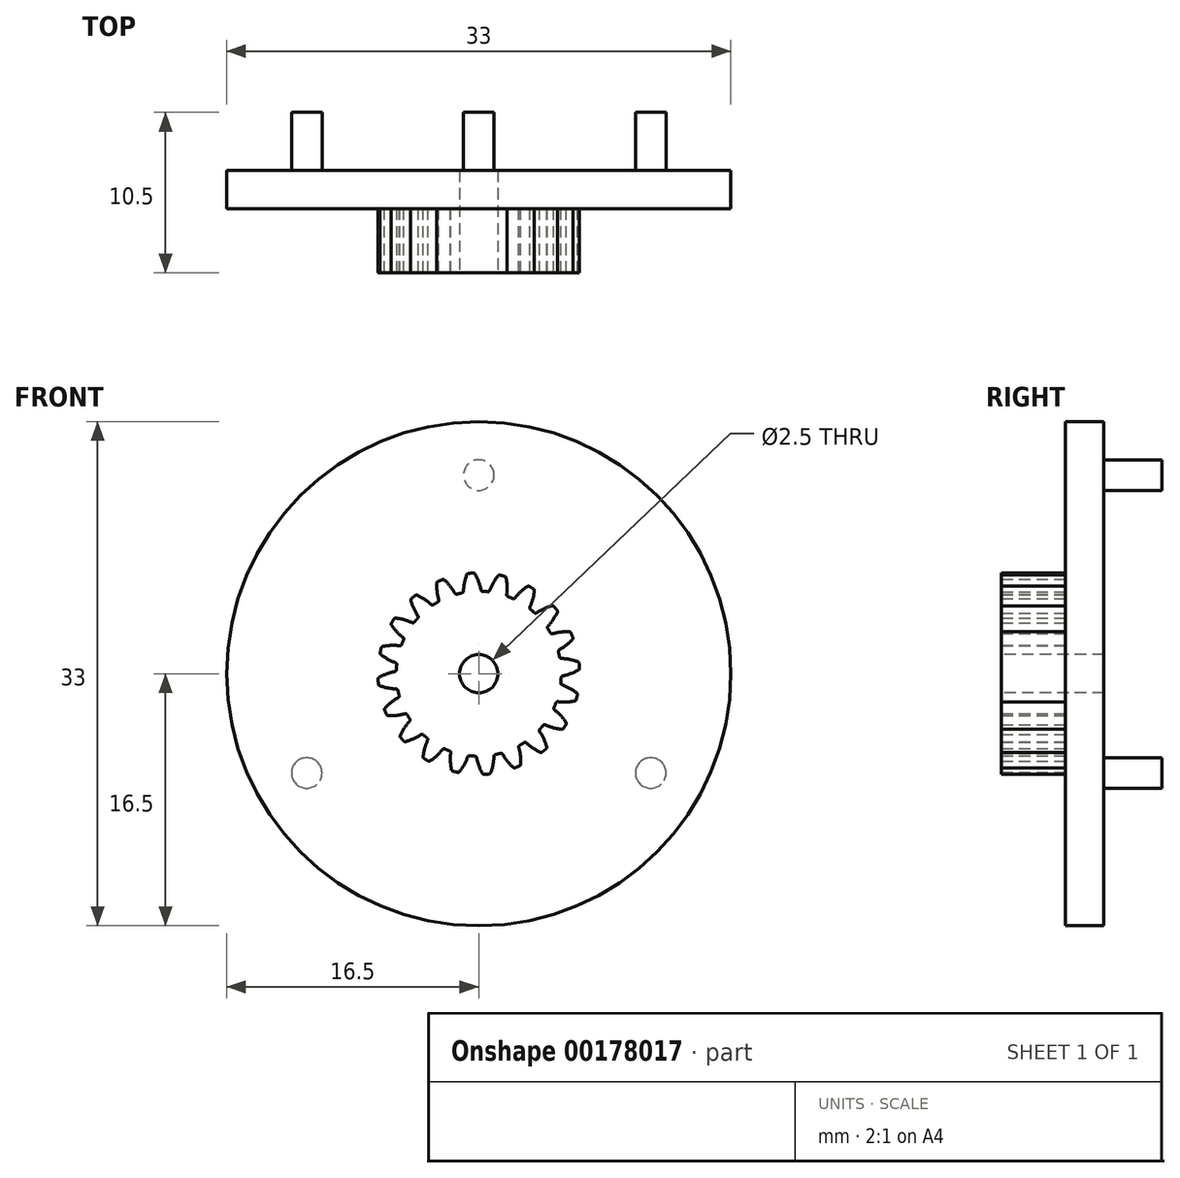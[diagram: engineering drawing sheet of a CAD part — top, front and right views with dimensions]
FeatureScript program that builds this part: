
annotation { "Feature Type Name" : "Feature", "Feature Type Description" : "" }
export const myFeature = defineFeature(function(context is Context, id is Id, definition is map)
    precondition{}
    {
        {
            var Q0;
            Q0=qCreatedBy(makeId("Front.planeOp"),FACE);
            var sketch = newSketch(context, id + "F0", { "sketchPlane" : qUnion([Q0])});
            skCircle(sketch, "E0", {"center": v(0, 0) * mm, "radius": 6 * mm, "construction": true});
            skCircle(sketch, "E1", {"center": v(0, 0) * mm, "radius": 5.4 * mm, "construction": true});
            skCircle(sketch, "E2", {"center": v(0, 0) * mm, "radius": 6.6 * mm, "construction": true});
            skLineSegment(sketch, "E3", {"start": v(0, 0) * mm, "end": v(0, 7.77) * mm, "construction": true});
            skPoint(sketch, "E4", {"position": v(0, 6) * mm});
            skLineSegment(sketch, "E5", {"start": v(0, 6) * mm, "end": v(-7.8, 6) * mm, "construction": true});
            skCircle(sketch, "E6.cCircle", {"center": v(0, 0) * mm, "radius": 7.77 * mm, "construction": true});
            skLineSegment(sketch, "E6.0", {"start": v(-0.61, 7.77) * mm, "end": v(0.61, 7.77) * mm, "construction": true});
            skLineSegment(sketch, "E6.1", {"start": v(0.61, 7.77) * mm, "end": v(1.82, 7.58) * mm, "construction": true});
            skLineSegment(sketch, "E6.2", {"start": v(1.82, 7.58) * mm, "end": v(2.98, 7.2) * mm, "construction": true});
            skLineSegment(sketch, "E6.3", {"start": v(2.98, 7.2) * mm, "end": v(4.07, 6.65) * mm, "construction": true});
            skLineSegment(sketch, "E6.4", {"start": v(4.07, 6.65) * mm, "end": v(5.06, 5.93) * mm, "construction": true});
            skLineSegment(sketch, "E6.5", {"start": v(5.06, 5.93) * mm, "end": v(5.93, 5.06) * mm, "construction": true});
            skLineSegment(sketch, "E6.6", {"start": v(5.93, 5.06) * mm, "end": v(6.65, 4.07) * mm, "construction": true});
            skLineSegment(sketch, "E6.7", {"start": v(6.65, 4.07) * mm, "end": v(7.2, 2.98) * mm, "construction": true});
            skLineSegment(sketch, "E6.8", {"start": v(7.2, 2.98) * mm, "end": v(7.58, 1.82) * mm, "construction": true});
            skLineSegment(sketch, "E6.9", {"start": v(7.58, 1.82) * mm, "end": v(7.77, 0.61) * mm, "construction": true});
            skLineSegment(sketch, "E6.10", {"start": v(7.77, 0.61) * mm, "end": v(7.77, -0.61) * mm, "construction": true});
            skLineSegment(sketch, "E6.11", {"start": v(7.77, -0.61) * mm, "end": v(7.58, -1.82) * mm, "construction": true});
            skLineSegment(sketch, "E6.12", {"start": v(7.58, -1.82) * mm, "end": v(7.2, -2.98) * mm, "construction": true});
            skLineSegment(sketch, "E6.13", {"start": v(7.2, -2.98) * mm, "end": v(6.65, -4.07) * mm, "construction": true});
            skLineSegment(sketch, "E6.14", {"start": v(6.65, -4.07) * mm, "end": v(5.93, -5.06) * mm, "construction": true});
            skLineSegment(sketch, "E6.15", {"start": v(5.93, -5.06) * mm, "end": v(5.06, -5.93) * mm, "construction": true});
            skLineSegment(sketch, "E6.16", {"start": v(5.06, -5.93) * mm, "end": v(4.07, -6.65) * mm, "construction": true});
            skLineSegment(sketch, "E6.17", {"start": v(4.07, -6.65) * mm, "end": v(2.98, -7.2) * mm, "construction": true});
            skLineSegment(sketch, "E6.18", {"start": v(2.98, -7.2) * mm, "end": v(1.82, -7.58) * mm, "construction": true});
            skLineSegment(sketch, "E6.19", {"start": v(1.82, -7.58) * mm, "end": v(0.61, -7.77) * mm, "construction": true});
            skLineSegment(sketch, "E6.20", {"start": v(0.61, -7.77) * mm, "end": v(-0.61, -7.77) * mm, "construction": true});
            skLineSegment(sketch, "E6.21", {"start": v(-0.61, -7.77) * mm, "end": v(-1.82, -7.58) * mm, "construction": true});
            skLineSegment(sketch, "E6.22", {"start": v(-1.82, -7.58) * mm, "end": v(-2.98, -7.2) * mm, "construction": true});
            skLineSegment(sketch, "E6.23", {"start": v(-2.98, -7.2) * mm, "end": v(-4.07, -6.65) * mm, "construction": true});
            skLineSegment(sketch, "E6.24", {"start": v(-4.07, -6.65) * mm, "end": v(-5.06, -5.93) * mm, "construction": true});
            skLineSegment(sketch, "E6.25", {"start": v(-5.06, -5.93) * mm, "end": v(-5.93, -5.06) * mm, "construction": true});
            skLineSegment(sketch, "E6.26", {"start": v(-5.93, -5.06) * mm, "end": v(-6.65, -4.07) * mm, "construction": true});
            skLineSegment(sketch, "E6.27", {"start": v(-6.65, -4.07) * mm, "end": v(-7.2, -2.98) * mm, "construction": true});
            skLineSegment(sketch, "E6.28", {"start": v(-7.2, -2.98) * mm, "end": v(-7.58, -1.82) * mm, "construction": true});
            skLineSegment(sketch, "E6.29", {"start": v(-7.58, -1.82) * mm, "end": v(-7.77, -0.61) * mm, "construction": true});
            skLineSegment(sketch, "E6.30", {"start": v(-7.77, -0.61) * mm, "end": v(-7.77, 0.61) * mm, "construction": true});
            skLineSegment(sketch, "E6.31", {"start": v(-7.77, 0.61) * mm, "end": v(-7.58, 1.82) * mm, "construction": true});
            skLineSegment(sketch, "E6.32", {"start": v(-7.58, 1.82) * mm, "end": v(-7.2, 2.98) * mm, "construction": true});
            skLineSegment(sketch, "E6.33", {"start": v(-7.2, 2.98) * mm, "end": v(-6.65, 4.07) * mm, "construction": true});
            skLineSegment(sketch, "E6.34", {"start": v(-6.65, 4.07) * mm, "end": v(-5.93, 5.06) * mm, "construction": true});
            skLineSegment(sketch, "E6.35", {"start": v(-5.93, 5.06) * mm, "end": v(-5.06, 5.93) * mm, "construction": true});
            skLineSegment(sketch, "E6.36", {"start": v(-5.06, 5.93) * mm, "end": v(-4.07, 6.65) * mm, "construction": true});
            skLineSegment(sketch, "E6.37", {"start": v(-4.07, 6.65) * mm, "end": v(-2.98, 7.2) * mm, "construction": true});
            skLineSegment(sketch, "E6.38", {"start": v(-2.98, 7.2) * mm, "end": v(-1.82, 7.58) * mm, "construction": true});
            skLineSegment(sketch, "E6.39", {"start": v(-1.82, 7.58) * mm, "end": v(-0.61, 7.77) * mm, "construction": true});
            skPoint(sketch, "E6.0.midPoint", {"position": v(0, 7.77) * mm});
            skLineSegment(sketch, "E7.0", {"start": v(0, 7.77) * mm, "end": v(1.22, 7.68) * mm, "construction": true});
            skLineSegment(sketch, "E7.1", {"start": v(1.22, 7.68) * mm, "end": v(2.4, 7.4) * mm, "construction": true});
            skLineSegment(sketch, "E7.2", {"start": v(2.4, 7.4) * mm, "end": v(3.53, 6.93) * mm, "construction": true});
            skLineSegment(sketch, "E7.3", {"start": v(3.53, 6.93) * mm, "end": v(4.57, 6.29) * mm, "construction": true});
            skLineSegment(sketch, "E7.4", {"start": v(4.57, 6.29) * mm, "end": v(5.5, 5.5) * mm, "construction": true});
            skLineSegment(sketch, "E7.5", {"start": v(5.5, 5.5) * mm, "end": v(6.29, 4.57) * mm, "construction": true});
            skLineSegment(sketch, "E7.6", {"start": v(6.29, 4.57) * mm, "end": v(6.93, 3.53) * mm, "construction": true});
            skLineSegment(sketch, "E7.7", {"start": v(6.93, 3.53) * mm, "end": v(7.4, 2.4) * mm, "construction": true});
            skLineSegment(sketch, "E7.8", {"start": v(7.4, 2.4) * mm, "end": v(7.68, 1.22) * mm, "construction": true});
            skLineSegment(sketch, "E7.9", {"start": v(7.68, 1.22) * mm, "end": v(7.77, 0) * mm, "construction": true});
            skLineSegment(sketch, "E7.10", {"start": v(7.77, 0) * mm, "end": v(7.68, -1.22) * mm, "construction": true});
            skLineSegment(sketch, "E7.11", {"start": v(7.68, -1.22) * mm, "end": v(7.4, -2.4) * mm, "construction": true});
            skLineSegment(sketch, "E7.12", {"start": v(7.4, -2.4) * mm, "end": v(6.93, -3.53) * mm, "construction": true});
            skLineSegment(sketch, "E7.13", {"start": v(6.93, -3.53) * mm, "end": v(6.29, -4.57) * mm, "construction": true});
            skLineSegment(sketch, "E7.14", {"start": v(6.29, -4.57) * mm, "end": v(5.5, -5.5) * mm, "construction": true});
            skLineSegment(sketch, "E7.15", {"start": v(5.5, -5.5) * mm, "end": v(4.57, -6.29) * mm, "construction": true});
            skLineSegment(sketch, "E7.16", {"start": v(4.57, -6.29) * mm, "end": v(3.53, -6.93) * mm, "construction": true});
            skLineSegment(sketch, "E7.17", {"start": v(3.53, -6.93) * mm, "end": v(2.4, -7.4) * mm, "construction": true});
            skLineSegment(sketch, "E7.18", {"start": v(2.4, -7.4) * mm, "end": v(1.22, -7.68) * mm, "construction": true});
            skLineSegment(sketch, "E7.19", {"start": v(1.22, -7.68) * mm, "end": v(0, -7.77) * mm, "construction": true});
            skLineSegment(sketch, "E7.20", {"start": v(0, -7.77) * mm, "end": v(-1.22, -7.68) * mm, "construction": true});
            skLineSegment(sketch, "E7.21", {"start": v(-1.22, -7.68) * mm, "end": v(-2.4, -7.4) * mm, "construction": true});
            skLineSegment(sketch, "E7.22", {"start": v(-2.4, -7.4) * mm, "end": v(-3.53, -6.93) * mm, "construction": true});
            skLineSegment(sketch, "E7.23", {"start": v(-3.53, -6.93) * mm, "end": v(-4.57, -6.29) * mm, "construction": true});
            skLineSegment(sketch, "E7.24", {"start": v(-4.57, -6.29) * mm, "end": v(-5.5, -5.5) * mm, "construction": true});
            skLineSegment(sketch, "E7.25", {"start": v(-5.5, -5.5) * mm, "end": v(-6.29, -4.57) * mm, "construction": true});
            skLineSegment(sketch, "E7.26", {"start": v(-6.29, -4.57) * mm, "end": v(-6.93, -3.53) * mm, "construction": true});
            skLineSegment(sketch, "E7.27", {"start": v(-6.93, -3.53) * mm, "end": v(-7.4, -2.4) * mm, "construction": true});
            skLineSegment(sketch, "E7.28", {"start": v(-7.4, -2.4) * mm, "end": v(-7.68, -1.22) * mm, "construction": true});
            skLineSegment(sketch, "E7.29", {"start": v(-7.68, -1.22) * mm, "end": v(-7.77, 0) * mm, "construction": true});
            skLineSegment(sketch, "E7.30", {"start": v(-7.77, 0) * mm, "end": v(-7.68, 1.22) * mm, "construction": true});
            skLineSegment(sketch, "E7.31", {"start": v(-7.68, 1.22) * mm, "end": v(-7.4, 2.4) * mm, "construction": true});
            skLineSegment(sketch, "E7.32", {"start": v(-7.4, 2.4) * mm, "end": v(-6.93, 3.53) * mm, "construction": true});
            skLineSegment(sketch, "E7.33", {"start": v(-6.93, 3.53) * mm, "end": v(-6.29, 4.57) * mm, "construction": true});
            skLineSegment(sketch, "E7.34", {"start": v(-6.29, 4.57) * mm, "end": v(-5.5, 5.5) * mm, "construction": true});
            skLineSegment(sketch, "E7.35", {"start": v(-5.5, 5.5) * mm, "end": v(-4.57, 6.29) * mm, "construction": true});
            skLineSegment(sketch, "E7.36", {"start": v(-4.57, 6.29) * mm, "end": v(-3.53, 6.93) * mm, "construction": true});
            skLineSegment(sketch, "E7.37", {"start": v(-3.53, 6.93) * mm, "end": v(-2.4, 7.4) * mm, "construction": true});
            skLineSegment(sketch, "E7.38", {"start": v(-2.4, 7.4) * mm, "end": v(-1.22, 7.68) * mm, "construction": true});
            skLineSegment(sketch, "E7.39", {"start": v(-1.22, 7.68) * mm, "end": v(0, 7.77) * mm, "construction": true});
            skLineSegment(sketch, "E8", {"start": v(0, 0) * mm, "end": v(-0.61, 7.77) * mm, "construction": true});
            skLineSegment(sketch, "E9", {"start": v(0, 6) * mm, "end": v(-7.35, 3.32) * mm, "construction": true});
            skCircle(sketch, "E10", {"center": v(0, 6) * mm, "radius": 3.6 * mm, "construction": true});
            skPoint(sketch, "E11", {"position": v(-3.38, 4.77) * mm});
            skCircle(sketch, "E12", {"center": v(-3.38, 4.77) * mm, "radius": 3.6 * mm, "construction": true});
            skArc(sketch, "E13", {"start": v(-0.24, 6.53) * mm, "mid": v(0, 6.02) * mm, "end": v(0.14, 5.49) * mm});
            skArc(sketch, "E14.MirrorCS", {"start": v(-0.78, 6.49) * mm, "mid": v(-0.93, 5.95) * mm, "end": v(-1, 5.4) * mm});
            skArc(sketch, "E15", {"start": v(-0.68, 6.56) * mm, "mid": v(-0.52, 6.58) * mm, "end": v(-0.35, 6.6) * mm});
            skArc(sketch, "E16", {"start": v(-1.1, 5.29) * mm, "mid": v(0.42, -5.38) * mm, "end": v(0.26, 5.4) * mm});
            skPoint(sketch, "E17.visualSharp", {"position": v(-1, 5.3) * mm});
            skArc(sketch, "E17.filletArc", {"start": v(-1.1, 5.29) * mm, "mid": v(-1.03, 5.33) * mm, "end": v(-1, 5.4) * mm});
            skPoint(sketch, "E18.visualSharp", {"position": v(0.16, 5.4) * mm});
            skArc(sketch, "E18.filletArc", {"start": v(0.14, 5.49) * mm, "mid": v(0.18, 5.42) * mm, "end": v(0.26, 5.4) * mm});
            skPoint(sketch, "E19.visualSharp", {"position": v(-0.76, 6.56) * mm});
            skArc(sketch, "E19.filletArc", {"start": v(-0.68, 6.56) * mm, "mid": v(-0.74, 6.54) * mm, "end": v(-0.78, 6.49) * mm});
            skPoint(sketch, "E20.visualSharp", {"position": v(-0.28, 6.6) * mm});
            skArc(sketch, "E20.filletArc", {"start": v(-0.24, 6.53) * mm, "mid": v(-0.29, 6.58) * mm, "end": v(-0.35, 6.6) * mm});
            skLineSegment(sketch, "E21", {"start": v(0, 0) * mm, "end": v(-1.44, 6.92) * mm, "construction": true});
            skPoint(sketch, "E22.1.0", {"position": v(-1.51, 5.18) * mm});
            skPoint(sketch, "E22.1.1", {"position": v(-1.85, 5.7) * mm});
            skArc(sketch, "E22.1.2", {"start": v(-2.25, 6.13) * mm, "mid": v(-1.87, 5.73) * mm, "end": v(-1.56, 5.27) * mm});
            skArc(sketch, "E22.1.3", {"start": v(-2.68, 6.03) * mm, "mid": v(-2.53, 6.1) * mm, "end": v(-2.37, 6.16) * mm});
            skPoint(sketch, "E22.1.4", {"position": v(-2.3, 6.18) * mm});
            skPoint(sketch, "E22.1.5", {"position": v(-2.6, 4.74) * mm});
            skArc(sketch, "E22.1.6", {"start": v(-2.75, 5.93) * mm, "mid": v(-2.73, 5.37) * mm, "end": v(-2.62, 4.83) * mm});
            skPoint(sketch, "E22.1.7", {"position": v(-2.74, 6) * mm});
            skArc(sketch, "E22.1.8", {"start": v(-1.56, 5.27) * mm, "mid": v(-1.5, 5.21) * mm, "end": v(-1.42, 5.2) * mm});
            skArc(sketch, "E22.1.9", {"start": v(-2.68, 6.03) * mm, "mid": v(-2.73, 6) * mm, "end": v(-2.75, 5.93) * mm});
            skArc(sketch, "E22.1.10", {"start": v(-2.68, 4.69) * mm, "mid": v(-2.63, 4.75) * mm, "end": v(-2.62, 4.83) * mm});
            skArc(sketch, "E22.1.11", {"start": v(-2.25, 6.13) * mm, "mid": v(-2.3, 6.16) * mm, "end": v(-2.37, 6.16) * mm});
            skPoint(sketch, "E22.2.0", {"position": v(-3.04, 4.46) * mm});
            skPoint(sketch, "E22.2.1", {"position": v(-3.53, 4.85) * mm});
            skArc(sketch, "E22.2.2", {"start": v(-4.03, 5.14) * mm, "mid": v(-3.55, 4.87) * mm, "end": v(-3.11, 4.53) * mm});
            skArc(sketch, "E22.2.3", {"start": v(-4.4, 4.91) * mm, "mid": v(-4.29, 5.02) * mm, "end": v(-4.16, 5.12) * mm});
            skPoint(sketch, "E22.2.4", {"position": v(-4.1, 5.17) * mm});
            skPoint(sketch, "E22.2.5", {"position": v(-3.93, 3.7) * mm});
            skArc(sketch, "E22.2.6", {"start": v(-4.45, 4.79) * mm, "mid": v(-4.25, 4.27) * mm, "end": v(-3.98, 3.78) * mm});
            skPoint(sketch, "E22.2.7", {"position": v(-4.46, 4.86) * mm});
            skArc(sketch, "E22.2.8", {"start": v(-3.11, 4.53) * mm, "mid": v(-3.04, 4.5) * mm, "end": v(-2.96, 4.51) * mm});
            skArc(sketch, "E22.2.9", {"start": v(-4.4, 4.91) * mm, "mid": v(-4.45, 4.85) * mm, "end": v(-4.45, 4.79) * mm});
            skArc(sketch, "E22.2.10", {"start": v(-4, 3.63) * mm, "mid": v(-3.96, 3.7) * mm, "end": v(-3.98, 3.78) * mm});
            skArc(sketch, "E22.2.11", {"start": v(-4.03, 5.14) * mm, "mid": v(-4.1, 5.15) * mm, "end": v(-4.16, 5.12) * mm});
            skPoint(sketch, "E22.3.0", {"position": v(-4.27, 3.3) * mm});
            skPoint(sketch, "E22.3.1", {"position": v(-4.85, 3.53) * mm});
            skArc(sketch, "E22.3.2", {"start": v(-5.43, 3.64) * mm, "mid": v(-4.88, 3.53) * mm, "end": v(-4.36, 3.34) * mm});
            skArc(sketch, "E22.3.3", {"start": v(-5.71, 3.3) * mm, "mid": v(-5.63, 3.45) * mm, "end": v(-5.54, 3.59) * mm});
            skPoint(sketch, "E22.3.4", {"position": v(-5.5, 3.65) * mm});
            skPoint(sketch, "E22.3.5", {"position": v(-4.88, 2.3) * mm});
            skArc(sketch, "E22.3.6", {"start": v(-5.7, 3.18) * mm, "mid": v(-5.36, 2.74) * mm, "end": v(-4.96, 2.36) * mm});
            skPoint(sketch, "E22.3.7", {"position": v(-5.75, 3.24) * mm});
            skArc(sketch, "E22.3.8", {"start": v(-4.36, 3.34) * mm, "mid": v(-4.28, 3.34) * mm, "end": v(-4.21, 3.38) * mm});
            skArc(sketch, "E22.3.9", {"start": v(-5.71, 3.3) * mm, "mid": v(-5.73, 3.24) * mm, "end": v(-5.7, 3.18) * mm});
            skArc(sketch, "E22.3.10", {"start": v(-4.92, 2.22) * mm, "mid": v(-4.92, 2.3) * mm, "end": v(-4.96, 2.36) * mm});
            skArc(sketch, "E22.3.11", {"start": v(-5.43, 3.64) * mm, "mid": v(-5.5, 3.63) * mm, "end": v(-5.54, 3.59) * mm});
            skPoint(sketch, "E22.4.0", {"position": v(-5.08, 1.82) * mm});
            skPoint(sketch, "E22.4.1", {"position": v(-5.7, 1.85) * mm});
            skArc(sketch, "E22.4.2", {"start": v(-6.28, 1.79) * mm, "mid": v(-5.73, 1.85) * mm, "end": v(-5.18, 1.83) * mm});
            skArc(sketch, "E22.4.3", {"start": v(-6.45, 1.38) * mm, "mid": v(-6.42, 1.54) * mm, "end": v(-6.38, 1.7) * mm});
            skPoint(sketch, "E22.4.4", {"position": v(-6.36, 1.77) * mm});
            skPoint(sketch, "E22.4.5", {"position": v(-5.36, 0.68) * mm});
            skArc(sketch, "E22.4.6", {"start": v(-6.41, 1.26) * mm, "mid": v(-5.95, 0.95) * mm, "end": v(-5.44, 0.72) * mm});
            skPoint(sketch, "E22.4.7", {"position": v(-6.47, 1.3) * mm});
            skArc(sketch, "E22.4.8", {"start": v(-5.18, 1.83) * mm, "mid": v(-5.1, 1.85) * mm, "end": v(-5.05, 1.91) * mm});
            skArc(sketch, "E22.4.9", {"start": v(-6.45, 1.38) * mm, "mid": v(-6.45, 1.31) * mm, "end": v(-6.41, 1.26) * mm});
            skArc(sketch, "E22.4.10", {"start": v(-5.37, 0.6) * mm, "mid": v(-5.38, 0.67) * mm, "end": v(-5.44, 0.72) * mm});
            skArc(sketch, "E22.4.11", {"start": v(-6.28, 1.79) * mm, "mid": v(-6.34, 1.76) * mm, "end": v(-6.38, 1.7) * mm});
            skPoint(sketch, "E22.5.0", {"position": v(-5.4, 0.16) * mm});
            skPoint(sketch, "E22.5.1", {"position": v(-6, 0) * mm});
            skArc(sketch, "E22.5.2", {"start": v(-6.53, -0.24) * mm, "mid": v(-6.02, 0) * mm, "end": v(-5.49, 0.14) * mm});
            skArc(sketch, "E22.5.3", {"start": v(-6.56, -0.68) * mm, "mid": v(-6.58, -0.52) * mm, "end": v(-6.6, -0.35) * mm});
            skPoint(sketch, "E22.5.4", {"position": v(-6.6, -0.28) * mm});
            skPoint(sketch, "E22.5.5", {"position": v(-5.3, -1) * mm});
            skArc(sketch, "E22.5.6", {"start": v(-6.49, -0.78) * mm, "mid": v(-5.95, -0.93) * mm, "end": v(-5.4, -1) * mm});
            skPoint(sketch, "E22.5.7", {"position": v(-6.56, -0.76) * mm});
            skArc(sketch, "E22.5.8", {"start": v(-5.49, 0.14) * mm, "mid": v(-5.42, 0.18) * mm, "end": v(-5.4, 0.26) * mm});
            skArc(sketch, "E22.5.9", {"start": v(-6.56, -0.68) * mm, "mid": v(-6.54, -0.74) * mm, "end": v(-6.49, -0.78) * mm});
            skArc(sketch, "E22.5.10", {"start": v(-5.29, -1.1) * mm, "mid": v(-5.33, -1.03) * mm, "end": v(-5.4, -1) * mm});
            skArc(sketch, "E22.5.11", {"start": v(-6.53, -0.24) * mm, "mid": v(-6.58, -0.29) * mm, "end": v(-6.6, -0.35) * mm});
            skPoint(sketch, "E22.6.0", {"position": v(-5.18, -1.51) * mm});
            skPoint(sketch, "E22.6.1", {"position": v(-5.7, -1.85) * mm});
            skArc(sketch, "E22.6.2", {"start": v(-6.13, -2.25) * mm, "mid": v(-5.73, -1.87) * mm, "end": v(-5.27, -1.56) * mm});
            skArc(sketch, "E22.6.3", {"start": v(-6.03, -2.68) * mm, "mid": v(-6.1, -2.53) * mm, "end": v(-6.16, -2.37) * mm});
            skPoint(sketch, "E22.6.4", {"position": v(-6.18, -2.3) * mm});
            skPoint(sketch, "E22.6.5", {"position": v(-4.74, -2.6) * mm});
            skArc(sketch, "E22.6.6", {"start": v(-5.93, -2.75) * mm, "mid": v(-5.37, -2.73) * mm, "end": v(-4.83, -2.62) * mm});
            skPoint(sketch, "E22.6.7", {"position": v(-6, -2.74) * mm});
            skArc(sketch, "E22.6.8", {"start": v(-5.27, -1.56) * mm, "mid": v(-5.21, -1.5) * mm, "end": v(-5.2, -1.42) * mm});
            skArc(sketch, "E22.6.9", {"start": v(-6.03, -2.68) * mm, "mid": v(-6, -2.73) * mm, "end": v(-5.93, -2.75) * mm});
            skArc(sketch, "E22.6.10", {"start": v(-4.69, -2.68) * mm, "mid": v(-4.75, -2.63) * mm, "end": v(-4.83, -2.62) * mm});
            skArc(sketch, "E22.6.11", {"start": v(-6.13, -2.25) * mm, "mid": v(-6.16, -2.3) * mm, "end": v(-6.16, -2.37) * mm});
            skPoint(sketch, "E22.7.0", {"position": v(-4.46, -3.04) * mm});
            skPoint(sketch, "E22.7.1", {"position": v(-4.85, -3.53) * mm});
            skArc(sketch, "E22.7.2", {"start": v(-5.14, -4.03) * mm, "mid": v(-4.87, -3.55) * mm, "end": v(-4.53, -3.11) * mm});
            skArc(sketch, "E22.7.3", {"start": v(-4.91, -4.4) * mm, "mid": v(-5.02, -4.29) * mm, "end": v(-5.12, -4.16) * mm});
            skPoint(sketch, "E22.7.4", {"position": v(-5.17, -4.1) * mm});
            skPoint(sketch, "E22.7.5", {"position": v(-3.7, -3.93) * mm});
            skArc(sketch, "E22.7.6", {"start": v(-4.79, -4.45) * mm, "mid": v(-4.27, -4.25) * mm, "end": v(-3.78, -3.98) * mm});
            skPoint(sketch, "E22.7.7", {"position": v(-4.86, -4.46) * mm});
            skArc(sketch, "E22.7.8", {"start": v(-4.53, -3.11) * mm, "mid": v(-4.5, -3.04) * mm, "end": v(-4.51, -2.96) * mm});
            skArc(sketch, "E22.7.9", {"start": v(-4.91, -4.4) * mm, "mid": v(-4.85, -4.45) * mm, "end": v(-4.79, -4.45) * mm});
            skArc(sketch, "E22.7.10", {"start": v(-3.63, -4) * mm, "mid": v(-3.7, -3.96) * mm, "end": v(-3.78, -3.98) * mm});
            skArc(sketch, "E22.7.11", {"start": v(-5.14, -4.03) * mm, "mid": v(-5.15, -4.1) * mm, "end": v(-5.12, -4.16) * mm});
            skPoint(sketch, "E22.8.0", {"position": v(-3.3, -4.27) * mm});
            skPoint(sketch, "E22.8.1", {"position": v(-3.53, -4.85) * mm});
            skArc(sketch, "E22.8.2", {"start": v(-3.64, -5.43) * mm, "mid": v(-3.53, -4.88) * mm, "end": v(-3.34, -4.36) * mm});
            skArc(sketch, "E22.8.3", {"start": v(-3.3, -5.71) * mm, "mid": v(-3.45, -5.63) * mm, "end": v(-3.59, -5.54) * mm});
            skPoint(sketch, "E22.8.4", {"position": v(-3.65, -5.5) * mm});
            skPoint(sketch, "E22.8.5", {"position": v(-2.3, -4.88) * mm});
            skArc(sketch, "E22.8.6", {"start": v(-3.18, -5.7) * mm, "mid": v(-2.74, -5.36) * mm, "end": v(-2.36, -4.96) * mm});
            skPoint(sketch, "E22.8.7", {"position": v(-3.24, -5.75) * mm});
            skArc(sketch, "E22.8.8", {"start": v(-3.34, -4.36) * mm, "mid": v(-3.34, -4.28) * mm, "end": v(-3.38, -4.21) * mm});
            skArc(sketch, "E22.8.9", {"start": v(-3.3, -5.71) * mm, "mid": v(-3.24, -5.73) * mm, "end": v(-3.18, -5.7) * mm});
            skArc(sketch, "E22.8.10", {"start": v(-2.22, -4.92) * mm, "mid": v(-2.3, -4.92) * mm, "end": v(-2.36, -4.96) * mm});
            skArc(sketch, "E22.8.11", {"start": v(-3.64, -5.43) * mm, "mid": v(-3.63, -5.5) * mm, "end": v(-3.59, -5.54) * mm});
            skPoint(sketch, "E22.9.0", {"position": v(-1.82, -5.08) * mm});
            skPoint(sketch, "E22.9.1", {"position": v(-1.85, -5.7) * mm});
            skArc(sketch, "E22.9.2", {"start": v(-1.79, -6.28) * mm, "mid": v(-1.85, -5.73) * mm, "end": v(-1.83, -5.18) * mm});
            skArc(sketch, "E22.9.3", {"start": v(-1.38, -6.45) * mm, "mid": v(-1.54, -6.42) * mm, "end": v(-1.7, -6.38) * mm});
            skPoint(sketch, "E22.9.4", {"position": v(-1.77, -6.36) * mm});
            skPoint(sketch, "E22.9.5", {"position": v(-0.68, -5.36) * mm});
            skArc(sketch, "E22.9.6", {"start": v(-1.26, -6.41) * mm, "mid": v(-0.95, -5.95) * mm, "end": v(-0.72, -5.44) * mm});
            skPoint(sketch, "E22.9.7", {"position": v(-1.3, -6.47) * mm});
            skArc(sketch, "E22.9.8", {"start": v(-1.83, -5.18) * mm, "mid": v(-1.85, -5.1) * mm, "end": v(-1.91, -5.05) * mm});
            skArc(sketch, "E22.9.9", {"start": v(-1.38, -6.45) * mm, "mid": v(-1.31, -6.45) * mm, "end": v(-1.26, -6.41) * mm});
            skArc(sketch, "E22.9.10", {"start": v(-0.6, -5.37) * mm, "mid": v(-0.67, -5.38) * mm, "end": v(-0.72, -5.44) * mm});
            skArc(sketch, "E22.9.11", {"start": v(-1.79, -6.28) * mm, "mid": v(-1.76, -6.34) * mm, "end": v(-1.7, -6.38) * mm});
            skPoint(sketch, "E22.10.0", {"position": v(-0.16, -5.4) * mm});
            skPoint(sketch, "E22.10.1", {"position": v(0, -6) * mm});
            skArc(sketch, "E22.10.2", {"start": v(0.24, -6.53) * mm, "mid": v(0, -6.02) * mm, "end": v(-0.14, -5.49) * mm});
            skArc(sketch, "E22.10.3", {"start": v(0.68, -6.56) * mm, "mid": v(0.52, -6.58) * mm, "end": v(0.35, -6.6) * mm});
            skPoint(sketch, "E22.10.4", {"position": v(0.28, -6.6) * mm});
            skPoint(sketch, "E22.10.5", {"position": v(1, -5.3) * mm});
            skArc(sketch, "E22.10.6", {"start": v(0.78, -6.49) * mm, "mid": v(0.93, -5.95) * mm, "end": v(1, -5.4) * mm});
            skPoint(sketch, "E22.10.7", {"position": v(0.76, -6.56) * mm});
            skArc(sketch, "E22.10.8", {"start": v(-0.14, -5.49) * mm, "mid": v(-0.18, -5.42) * mm, "end": v(-0.26, -5.4) * mm});
            skArc(sketch, "E22.10.9", {"start": v(0.68, -6.56) * mm, "mid": v(0.74, -6.54) * mm, "end": v(0.78, -6.49) * mm});
            skArc(sketch, "E22.10.10", {"start": v(1.1, -5.29) * mm, "mid": v(1.03, -5.33) * mm, "end": v(1, -5.4) * mm});
            skArc(sketch, "E22.10.11", {"start": v(0.24, -6.53) * mm, "mid": v(0.29, -6.58) * mm, "end": v(0.35, -6.6) * mm});
            skPoint(sketch, "E22.11.0", {"position": v(1.51, -5.18) * mm});
            skPoint(sketch, "E22.11.1", {"position": v(1.85, -5.7) * mm});
            skArc(sketch, "E22.11.2", {"start": v(2.25, -6.13) * mm, "mid": v(1.87, -5.73) * mm, "end": v(1.56, -5.27) * mm});
            skArc(sketch, "E22.11.3", {"start": v(2.68, -6.03) * mm, "mid": v(2.53, -6.1) * mm, "end": v(2.37, -6.16) * mm});
            skPoint(sketch, "E22.11.4", {"position": v(2.3, -6.18) * mm});
            skPoint(sketch, "E22.11.5", {"position": v(2.6, -4.74) * mm});
            skArc(sketch, "E22.11.6", {"start": v(2.75, -5.93) * mm, "mid": v(2.73, -5.37) * mm, "end": v(2.62, -4.83) * mm});
            skPoint(sketch, "E22.11.7", {"position": v(2.74, -6) * mm});
            skArc(sketch, "E22.11.8", {"start": v(1.56, -5.27) * mm, "mid": v(1.5, -5.21) * mm, "end": v(1.42, -5.2) * mm});
            skArc(sketch, "E22.11.9", {"start": v(2.68, -6.03) * mm, "mid": v(2.73, -6) * mm, "end": v(2.75, -5.93) * mm});
            skArc(sketch, "E22.11.10", {"start": v(2.68, -4.69) * mm, "mid": v(2.63, -4.75) * mm, "end": v(2.62, -4.83) * mm});
            skArc(sketch, "E22.11.11", {"start": v(2.25, -6.13) * mm, "mid": v(2.3, -6.16) * mm, "end": v(2.37, -6.16) * mm});
            skPoint(sketch, "E22.12.0", {"position": v(3.04, -4.46) * mm});
            skPoint(sketch, "E22.12.1", {"position": v(3.53, -4.85) * mm});
            skArc(sketch, "E22.12.2", {"start": v(4.03, -5.14) * mm, "mid": v(3.55, -4.87) * mm, "end": v(3.11, -4.53) * mm});
            skArc(sketch, "E22.12.3", {"start": v(4.4, -4.91) * mm, "mid": v(4.29, -5.02) * mm, "end": v(4.16, -5.12) * mm});
            skPoint(sketch, "E22.12.4", {"position": v(4.1, -5.17) * mm});
            skPoint(sketch, "E22.12.5", {"position": v(3.93, -3.7) * mm});
            skArc(sketch, "E22.12.6", {"start": v(4.45, -4.79) * mm, "mid": v(4.25, -4.27) * mm, "end": v(3.98, -3.78) * mm});
            skPoint(sketch, "E22.12.7", {"position": v(4.46, -4.86) * mm});
            skArc(sketch, "E22.12.8", {"start": v(3.11, -4.53) * mm, "mid": v(3.04, -4.5) * mm, "end": v(2.96, -4.51) * mm});
            skArc(sketch, "E22.12.9", {"start": v(4.4, -4.91) * mm, "mid": v(4.45, -4.85) * mm, "end": v(4.45, -4.79) * mm});
            skArc(sketch, "E22.12.10", {"start": v(4, -3.63) * mm, "mid": v(3.96, -3.7) * mm, "end": v(3.98, -3.78) * mm});
            skArc(sketch, "E22.12.11", {"start": v(4.03, -5.14) * mm, "mid": v(4.1, -5.15) * mm, "end": v(4.16, -5.12) * mm});
            skPoint(sketch, "E22.13.0", {"position": v(4.27, -3.3) * mm});
            skPoint(sketch, "E22.13.1", {"position": v(4.85, -3.53) * mm});
            skArc(sketch, "E22.13.2", {"start": v(5.43, -3.64) * mm, "mid": v(4.88, -3.53) * mm, "end": v(4.36, -3.34) * mm});
            skArc(sketch, "E22.13.3", {"start": v(5.71, -3.3) * mm, "mid": v(5.63, -3.45) * mm, "end": v(5.54, -3.59) * mm});
            skPoint(sketch, "E22.13.4", {"position": v(5.5, -3.65) * mm});
            skPoint(sketch, "E22.13.5", {"position": v(4.88, -2.3) * mm});
            skArc(sketch, "E22.13.6", {"start": v(5.7, -3.18) * mm, "mid": v(5.36, -2.74) * mm, "end": v(4.96, -2.36) * mm});
            skPoint(sketch, "E22.13.7", {"position": v(5.75, -3.24) * mm});
            skArc(sketch, "E22.13.8", {"start": v(4.36, -3.34) * mm, "mid": v(4.28, -3.34) * mm, "end": v(4.21, -3.38) * mm});
            skArc(sketch, "E22.13.9", {"start": v(5.71, -3.3) * mm, "mid": v(5.73, -3.24) * mm, "end": v(5.7, -3.18) * mm});
            skArc(sketch, "E22.13.10", {"start": v(4.92, -2.22) * mm, "mid": v(4.92, -2.3) * mm, "end": v(4.96, -2.36) * mm});
            skArc(sketch, "E22.13.11", {"start": v(5.43, -3.64) * mm, "mid": v(5.5, -3.63) * mm, "end": v(5.54, -3.59) * mm});
            skPoint(sketch, "E22.14.0", {"position": v(5.08, -1.82) * mm});
            skPoint(sketch, "E22.14.1", {"position": v(5.7, -1.85) * mm});
            skArc(sketch, "E22.14.2", {"start": v(6.28, -1.79) * mm, "mid": v(5.73, -1.85) * mm, "end": v(5.18, -1.83) * mm});
            skArc(sketch, "E22.14.3", {"start": v(6.45, -1.38) * mm, "mid": v(6.42, -1.54) * mm, "end": v(6.38, -1.7) * mm});
            skPoint(sketch, "E22.14.4", {"position": v(6.36, -1.77) * mm});
            skPoint(sketch, "E22.14.5", {"position": v(5.36, -0.68) * mm});
            skArc(sketch, "E22.14.6", {"start": v(6.41, -1.26) * mm, "mid": v(5.95, -0.95) * mm, "end": v(5.44, -0.72) * mm});
            skPoint(sketch, "E22.14.7", {"position": v(6.47, -1.3) * mm});
            skArc(sketch, "E22.14.8", {"start": v(5.18, -1.83) * mm, "mid": v(5.1, -1.85) * mm, "end": v(5.05, -1.91) * mm});
            skArc(sketch, "E22.14.9", {"start": v(6.45, -1.38) * mm, "mid": v(6.45, -1.31) * mm, "end": v(6.41, -1.26) * mm});
            skArc(sketch, "E22.14.10", {"start": v(5.37, -0.6) * mm, "mid": v(5.38, -0.67) * mm, "end": v(5.44, -0.72) * mm});
            skArc(sketch, "E22.14.11", {"start": v(6.28, -1.79) * mm, "mid": v(6.34, -1.76) * mm, "end": v(6.38, -1.7) * mm});
            skPoint(sketch, "E22.15.0", {"position": v(5.4, -0.16) * mm});
            skPoint(sketch, "E22.15.1", {"position": v(6, 0) * mm});
            skArc(sketch, "E22.15.2", {"start": v(6.53, 0.24) * mm, "mid": v(6.02, 0) * mm, "end": v(5.49, -0.14) * mm});
            skArc(sketch, "E22.15.3", {"start": v(6.56, 0.68) * mm, "mid": v(6.58, 0.52) * mm, "end": v(6.6, 0.35) * mm});
            skPoint(sketch, "E22.15.4", {"position": v(6.6, 0.28) * mm});
            skPoint(sketch, "E22.15.5", {"position": v(5.3, 1) * mm});
            skArc(sketch, "E22.15.6", {"start": v(6.49, 0.78) * mm, "mid": v(5.95, 0.93) * mm, "end": v(5.4, 1) * mm});
            skPoint(sketch, "E22.15.7", {"position": v(6.56, 0.76) * mm});
            skArc(sketch, "E22.15.8", {"start": v(5.49, -0.14) * mm, "mid": v(5.42, -0.18) * mm, "end": v(5.4, -0.26) * mm});
            skArc(sketch, "E22.15.9", {"start": v(6.56, 0.68) * mm, "mid": v(6.54, 0.74) * mm, "end": v(6.49, 0.78) * mm});
            skArc(sketch, "E22.15.10", {"start": v(5.29, 1.1) * mm, "mid": v(5.33, 1.03) * mm, "end": v(5.4, 1) * mm});
            skArc(sketch, "E22.15.11", {"start": v(6.53, 0.24) * mm, "mid": v(6.58, 0.29) * mm, "end": v(6.6, 0.35) * mm});
            skPoint(sketch, "E22.16.0", {"position": v(5.18, 1.51) * mm});
            skPoint(sketch, "E22.16.1", {"position": v(5.7, 1.85) * mm});
            skArc(sketch, "E22.16.2", {"start": v(6.13, 2.25) * mm, "mid": v(5.73, 1.87) * mm, "end": v(5.27, 1.56) * mm});
            skArc(sketch, "E22.16.3", {"start": v(6.03, 2.68) * mm, "mid": v(6.1, 2.53) * mm, "end": v(6.16, 2.37) * mm});
            skPoint(sketch, "E22.16.4", {"position": v(6.18, 2.3) * mm});
            skPoint(sketch, "E22.16.5", {"position": v(4.74, 2.6) * mm});
            skArc(sketch, "E22.16.6", {"start": v(5.93, 2.75) * mm, "mid": v(5.37, 2.73) * mm, "end": v(4.83, 2.62) * mm});
            skPoint(sketch, "E22.16.7", {"position": v(6, 2.74) * mm});
            skArc(sketch, "E22.16.8", {"start": v(5.27, 1.56) * mm, "mid": v(5.21, 1.5) * mm, "end": v(5.2, 1.42) * mm});
            skArc(sketch, "E22.16.9", {"start": v(6.03, 2.68) * mm, "mid": v(6, 2.73) * mm, "end": v(5.93, 2.75) * mm});
            skArc(sketch, "E22.16.10", {"start": v(4.69, 2.68) * mm, "mid": v(4.75, 2.63) * mm, "end": v(4.83, 2.62) * mm});
            skArc(sketch, "E22.16.11", {"start": v(6.13, 2.25) * mm, "mid": v(6.16, 2.3) * mm, "end": v(6.16, 2.37) * mm});
            skPoint(sketch, "E22.17.0", {"position": v(4.46, 3.04) * mm});
            skPoint(sketch, "E22.17.1", {"position": v(4.85, 3.53) * mm});
            skArc(sketch, "E22.17.2", {"start": v(5.14, 4.03) * mm, "mid": v(4.87, 3.55) * mm, "end": v(4.53, 3.11) * mm});
            skArc(sketch, "E22.17.3", {"start": v(4.91, 4.4) * mm, "mid": v(5.02, 4.29) * mm, "end": v(5.12, 4.16) * mm});
            skPoint(sketch, "E22.17.4", {"position": v(5.17, 4.1) * mm});
            skPoint(sketch, "E22.17.5", {"position": v(3.7, 3.93) * mm});
            skArc(sketch, "E22.17.6", {"start": v(4.79, 4.45) * mm, "mid": v(4.27, 4.25) * mm, "end": v(3.78, 3.98) * mm});
            skPoint(sketch, "E22.17.7", {"position": v(4.86, 4.46) * mm});
            skArc(sketch, "E22.17.8", {"start": v(4.53, 3.11) * mm, "mid": v(4.5, 3.04) * mm, "end": v(4.51, 2.96) * mm});
            skArc(sketch, "E22.17.9", {"start": v(4.91, 4.4) * mm, "mid": v(4.85, 4.45) * mm, "end": v(4.79, 4.45) * mm});
            skArc(sketch, "E22.17.10", {"start": v(3.63, 4) * mm, "mid": v(3.7, 3.96) * mm, "end": v(3.78, 3.98) * mm});
            skArc(sketch, "E22.17.11", {"start": v(5.14, 4.03) * mm, "mid": v(5.15, 4.1) * mm, "end": v(5.12, 4.16) * mm});
            skPoint(sketch, "E22.18.0", {"position": v(3.3, 4.27) * mm});
            skPoint(sketch, "E22.18.1", {"position": v(3.53, 4.85) * mm});
            skArc(sketch, "E22.18.2", {"start": v(3.64, 5.43) * mm, "mid": v(3.53, 4.88) * mm, "end": v(3.34, 4.36) * mm});
            skArc(sketch, "E22.18.3", {"start": v(3.3, 5.71) * mm, "mid": v(3.45, 5.63) * mm, "end": v(3.59, 5.54) * mm});
            skPoint(sketch, "E22.18.4", {"position": v(3.65, 5.5) * mm});
            skPoint(sketch, "E22.18.5", {"position": v(2.3, 4.88) * mm});
            skArc(sketch, "E22.18.6", {"start": v(3.18, 5.7) * mm, "mid": v(2.74, 5.36) * mm, "end": v(2.36, 4.96) * mm});
            skPoint(sketch, "E22.18.7", {"position": v(3.24, 5.75) * mm});
            skArc(sketch, "E22.18.8", {"start": v(3.34, 4.36) * mm, "mid": v(3.34, 4.28) * mm, "end": v(3.38, 4.21) * mm});
            skArc(sketch, "E22.18.9", {"start": v(3.3, 5.71) * mm, "mid": v(3.24, 5.73) * mm, "end": v(3.18, 5.7) * mm});
            skArc(sketch, "E22.18.10", {"start": v(2.22, 4.92) * mm, "mid": v(2.3, 4.92) * mm, "end": v(2.36, 4.96) * mm});
            skArc(sketch, "E22.18.11", {"start": v(3.64, 5.43) * mm, "mid": v(3.63, 5.5) * mm, "end": v(3.59, 5.54) * mm});
            skPoint(sketch, "E22.19.0", {"position": v(1.82, 5.08) * mm});
            skPoint(sketch, "E22.19.1", {"position": v(1.85, 5.7) * mm});
            skArc(sketch, "E22.19.2", {"start": v(1.79, 6.28) * mm, "mid": v(1.85, 5.73) * mm, "end": v(1.83, 5.18) * mm});
            skArc(sketch, "E22.19.3", {"start": v(1.38, 6.45) * mm, "mid": v(1.54, 6.42) * mm, "end": v(1.7, 6.38) * mm});
            skPoint(sketch, "E22.19.4", {"position": v(1.77, 6.36) * mm});
            skPoint(sketch, "E22.19.5", {"position": v(0.68, 5.36) * mm});
            skArc(sketch, "E22.19.6", {"start": v(1.26, 6.41) * mm, "mid": v(0.95, 5.95) * mm, "end": v(0.72, 5.44) * mm});
            skPoint(sketch, "E22.19.7", {"position": v(1.3, 6.47) * mm});
            skArc(sketch, "E22.19.8", {"start": v(1.83, 5.18) * mm, "mid": v(1.85, 5.1) * mm, "end": v(1.91, 5.05) * mm});
            skArc(sketch, "E22.19.9", {"start": v(1.38, 6.45) * mm, "mid": v(1.31, 6.45) * mm, "end": v(1.26, 6.41) * mm});
            skArc(sketch, "E22.19.10", {"start": v(0.6, 5.37) * mm, "mid": v(0.67, 5.38) * mm, "end": v(0.72, 5.44) * mm});
            skArc(sketch, "E22.19.11", {"start": v(1.79, 6.28) * mm, "mid": v(1.76, 6.34) * mm, "end": v(1.7, 6.38) * mm});
            skSolve(sketch);
        }
        {
            var Q0;
            Q0=qSketchRegion(id+"F0",true);
            extrude(context, id + "F1", {"entities" : qUnion([Q0]), "depth" : 4.2 * mm});
        }
        {
            var Q0;
            Q0=qCreatedBy(makeId("Front.planeOp"),FACE);
            var sketch = newSketch(context, id + "F2", { "sketchPlane" : qUnion([Q0])});
            skCircle(sketch, "E23", {"center": v(0, 0) * mm, "radius": 16.5 * mm});
            skSolve(sketch);
        }
        {
            var Q0;
            Q0=qSketchRegion(id+"F2",true);
            extrude(context, id + "F3", {"entities" : qUnion([Q0]), "operationType" : NewBodyOperationType.ADD, "oppositeDirection" : true, "depth" : 2.5 * mm});
        }
        {
            var Q0;
            Q0=makeQuery(id+"F1.opExtrude","CAP_FACE",FACE,{"disambiguationData":[OSD([sQuery(id+"F0.wireOp",EDGE,"E13"),sQuery(id+"F0.wireOp",EDGE,"E14.MirrorCS"),sQuery(id+"F0.wireOp",EDGE,"E15"),sQuery(id+"F0.wireOp",EDGE,"E16"),sQuery(id+"F0.wireOp",EDGE,"E17.filletArc"),sQuery(id+"F0.wireOp",EDGE,"E18.filletArc"),sQuery(id+"F0.wireOp",EDGE,"E19.filletArc"),sQuery(id+"F0.wireOp",EDGE,"E20.filletArc"),sQuery(id+"F0.wireOp",EDGE,"E22.1.2"),sQuery(id+"F0.wireOp",EDGE,"E22.1.3"),sQuery(id+"F0.wireOp",EDGE,"E22.1.6"),sQuery(id+"F0.wireOp",EDGE,"E22.1.8"),sQuery(id+"F0.wireOp",EDGE,"E22.1.9"),sQuery(id+"F0.wireOp",EDGE,"E22.1.10"),sQuery(id+"F0.wireOp",EDGE,"E22.1.11"),sQuery(id+"F0.wireOp",EDGE,"E22.2.2"),sQuery(id+"F0.wireOp",EDGE,"E22.2.3"),sQuery(id+"F0.wireOp",EDGE,"E22.2.6"),sQuery(id+"F0.wireOp",EDGE,"E22.2.8"),sQuery(id+"F0.wireOp",EDGE,"E22.2.9"),sQuery(id+"F0.wireOp",EDGE,"E22.2.10"),sQuery(id+"F0.wireOp",EDGE,"E22.2.11"),sQuery(id+"F0.wireOp",EDGE,"E22.3.2"),sQuery(id+"F0.wireOp",EDGE,"E22.3.3"),sQuery(id+"F0.wireOp",EDGE,"E22.3.6"),sQuery(id+"F0.wireOp",EDGE,"E22.3.8"),sQuery(id+"F0.wireOp",EDGE,"E22.3.9"),sQuery(id+"F0.wireOp",EDGE,"E22.3.10"),sQuery(id+"F0.wireOp",EDGE,"E22.3.11"),sQuery(id+"F0.wireOp",EDGE,"E22.4.2"),sQuery(id+"F0.wireOp",EDGE,"E22.4.3"),sQuery(id+"F0.wireOp",EDGE,"E22.4.6"),sQuery(id+"F0.wireOp",EDGE,"E22.4.8"),sQuery(id+"F0.wireOp",EDGE,"E22.4.9"),sQuery(id+"F0.wireOp",EDGE,"E22.4.10"),sQuery(id+"F0.wireOp",EDGE,"E22.4.11"),sQuery(id+"F0.wireOp",EDGE,"E22.5.2"),sQuery(id+"F0.wireOp",EDGE,"E22.5.3"),sQuery(id+"F0.wireOp",EDGE,"E22.5.6"),sQuery(id+"F0.wireOp",EDGE,"E22.5.8"),sQuery(id+"F0.wireOp",EDGE,"E22.5.9"),sQuery(id+"F0.wireOp",EDGE,"E22.5.10"),sQuery(id+"F0.wireOp",EDGE,"E22.5.11"),sQuery(id+"F0.wireOp",EDGE,"E22.6.2"),sQuery(id+"F0.wireOp",EDGE,"E22.6.3"),sQuery(id+"F0.wireOp",EDGE,"E22.6.6"),sQuery(id+"F0.wireOp",EDGE,"E22.6.8"),sQuery(id+"F0.wireOp",EDGE,"E22.6.9"),sQuery(id+"F0.wireOp",EDGE,"E22.6.10"),sQuery(id+"F0.wireOp",EDGE,"E22.6.11"),sQuery(id+"F0.wireOp",EDGE,"E22.7.2"),sQuery(id+"F0.wireOp",EDGE,"E22.7.3"),sQuery(id+"F0.wireOp",EDGE,"E22.7.6"),sQuery(id+"F0.wireOp",EDGE,"E22.7.8"),sQuery(id+"F0.wireOp",EDGE,"E22.7.9"),sQuery(id+"F0.wireOp",EDGE,"E22.7.10"),sQuery(id+"F0.wireOp",EDGE,"E22.7.11"),sQuery(id+"F0.wireOp",EDGE,"E22.8.2"),sQuery(id+"F0.wireOp",EDGE,"E22.8.3"),sQuery(id+"F0.wireOp",EDGE,"E22.8.6"),sQuery(id+"F0.wireOp",EDGE,"E22.8.8"),sQuery(id+"F0.wireOp",EDGE,"E22.8.9"),sQuery(id+"F0.wireOp",EDGE,"E22.8.10"),sQuery(id+"F0.wireOp",EDGE,"E22.8.11"),sQuery(id+"F0.wireOp",EDGE,"E22.9.2"),sQuery(id+"F0.wireOp",EDGE,"E22.9.3"),sQuery(id+"F0.wireOp",EDGE,"E22.9.6"),sQuery(id+"F0.wireOp",EDGE,"E22.9.8"),sQuery(id+"F0.wireOp",EDGE,"E22.9.9"),sQuery(id+"F0.wireOp",EDGE,"E22.9.10"),sQuery(id+"F0.wireOp",EDGE,"E22.9.11"),sQuery(id+"F0.wireOp",EDGE,"E22.10.2"),sQuery(id+"F0.wireOp",EDGE,"E22.10.3"),sQuery(id+"F0.wireOp",EDGE,"E22.10.6"),sQuery(id+"F0.wireOp",EDGE,"E22.10.8"),sQuery(id+"F0.wireOp",EDGE,"E22.10.9"),sQuery(id+"F0.wireOp",EDGE,"E22.10.10"),sQuery(id+"F0.wireOp",EDGE,"E22.10.11"),sQuery(id+"F0.wireOp",EDGE,"E22.11.2"),sQuery(id+"F0.wireOp",EDGE,"E22.11.3"),sQuery(id+"F0.wireOp",EDGE,"E22.11.6"),sQuery(id+"F0.wireOp",EDGE,"E22.11.8"),sQuery(id+"F0.wireOp",EDGE,"E22.11.9"),sQuery(id+"F0.wireOp",EDGE,"E22.11.10"),sQuery(id+"F0.wireOp",EDGE,"E22.11.11"),sQuery(id+"F0.wireOp",EDGE,"E22.12.2"),sQuery(id+"F0.wireOp",EDGE,"E22.12.3"),sQuery(id+"F0.wireOp",EDGE,"E22.12.6"),sQuery(id+"F0.wireOp",EDGE,"E22.12.8"),sQuery(id+"F0.wireOp",EDGE,"E22.12.9"),sQuery(id+"F0.wireOp",EDGE,"E22.12.10"),sQuery(id+"F0.wireOp",EDGE,"E22.12.11"),sQuery(id+"F0.wireOp",EDGE,"E22.13.2"),sQuery(id+"F0.wireOp",EDGE,"E22.13.3"),sQuery(id+"F0.wireOp",EDGE,"E22.13.6"),sQuery(id+"F0.wireOp",EDGE,"E22.13.8"),sQuery(id+"F0.wireOp",EDGE,"E22.13.9"),sQuery(id+"F0.wireOp",EDGE,"E22.13.10"),sQuery(id+"F0.wireOp",EDGE,"E22.13.11"),sQuery(id+"F0.wireOp",EDGE,"E22.14.2"),sQuery(id+"F0.wireOp",EDGE,"E22.14.3"),sQuery(id+"F0.wireOp",EDGE,"E22.14.6"),sQuery(id+"F0.wireOp",EDGE,"E22.14.8"),sQuery(id+"F0.wireOp",EDGE,"E22.14.9"),sQuery(id+"F0.wireOp",EDGE,"E22.14.10"),sQuery(id+"F0.wireOp",EDGE,"E22.14.11"),sQuery(id+"F0.wireOp",EDGE,"E22.15.2"),sQuery(id+"F0.wireOp",EDGE,"E22.15.3"),sQuery(id+"F0.wireOp",EDGE,"E22.15.6"),sQuery(id+"F0.wireOp",EDGE,"E22.15.8"),sQuery(id+"F0.wireOp",EDGE,"E22.15.9"),sQuery(id+"F0.wireOp",EDGE,"E22.15.10"),sQuery(id+"F0.wireOp",EDGE,"E22.15.11"),sQuery(id+"F0.wireOp",EDGE,"E22.16.2"),sQuery(id+"F0.wireOp",EDGE,"E22.16.3"),sQuery(id+"F0.wireOp",EDGE,"E22.16.6"),sQuery(id+"F0.wireOp",EDGE,"E22.16.8"),sQuery(id+"F0.wireOp",EDGE,"E22.16.9"),sQuery(id+"F0.wireOp",EDGE,"E22.16.10"),sQuery(id+"F0.wireOp",EDGE,"E22.16.11"),sQuery(id+"F0.wireOp",EDGE,"E22.17.2"),sQuery(id+"F0.wireOp",EDGE,"E22.17.3"),sQuery(id+"F0.wireOp",EDGE,"E22.17.6"),sQuery(id+"F0.wireOp",EDGE,"E22.17.8"),sQuery(id+"F0.wireOp",EDGE,"E22.17.9"),sQuery(id+"F0.wireOp",EDGE,"E22.17.10"),sQuery(id+"F0.wireOp",EDGE,"E22.17.11"),sQuery(id+"F0.wireOp",EDGE,"E22.18.2"),sQuery(id+"F0.wireOp",EDGE,"E22.18.3"),sQuery(id+"F0.wireOp",EDGE,"E22.18.6"),sQuery(id+"F0.wireOp",EDGE,"E22.18.8"),sQuery(id+"F0.wireOp",EDGE,"E22.18.9"),sQuery(id+"F0.wireOp",EDGE,"E22.18.10"),sQuery(id+"F0.wireOp",EDGE,"E22.18.11"),sQuery(id+"F0.wireOp",EDGE,"E22.19.2"),sQuery(id+"F0.wireOp",EDGE,"E22.19.3"),sQuery(id+"F0.wireOp",EDGE,"E22.19.6"),sQuery(id+"F0.wireOp",EDGE,"E22.19.8"),sQuery(id+"F0.wireOp",EDGE,"E22.19.9"),sQuery(id+"F0.wireOp",EDGE,"E22.19.10"),sQuery(id+"F0.wireOp",EDGE,"E22.19.11")])],"isStart":false});
            var sketch = newSketch(context, id + "F4", { "sketchPlane" : qUnion([Q0])});
            skCircle(sketch, "E24", {"center": v(0, 0) * mm, "radius": 1.25 * mm});
            skSolve(sketch);
        }
        {
            var Q0;
            Q0=qSketchRegion(id+"F4",true);
            extrude(context, id + "F5", {"entities" : qUnion([Q0]), "operationType" : NewBodyOperationType.REMOVE, "oppositeDirection" : true, "depth" : 25 * mm});
        }
        {
            var Q0;
            Q0=makeQuery(id+"F3.opExtrude","CAP_FACE",FACE,{"disambiguationData":[OSD([sQuery(id+"F2.wireOp",EDGE,"E23")])],"isStart":false});
            var sketch = newSketch(context, id + "F6", { "sketchPlane" : qUnion([Q0])});
            skLineSegment(sketch, "E25", {"start": v(0, 0) * mm, "end": v(0, 16.5) * mm, "construction": true});
            skCircle(sketch, "E26", {"center": v(0, 13) * mm, "radius": 1 * mm});
            skCircle(sketch, "E27.1.0", {"center": v(-11.26, -6.5) * mm, "radius": 1 * mm});
            skCircle(sketch, "E27.2.0", {"center": v(11.26, -6.5) * mm, "radius": 1 * mm});
            skPoint(sketch, "E27.center", {"position": v(0, 0) * mm});
            skSolve(sketch);
        }
        {
            var Q0;
            Q0=qSketchRegion(id+"F6",true);
            extrude(context, id + "F7", {"entities" : qUnion([Q0]), "operationType" : NewBodyOperationType.ADD, "depth" : 3.8 * mm});
        }
    });
